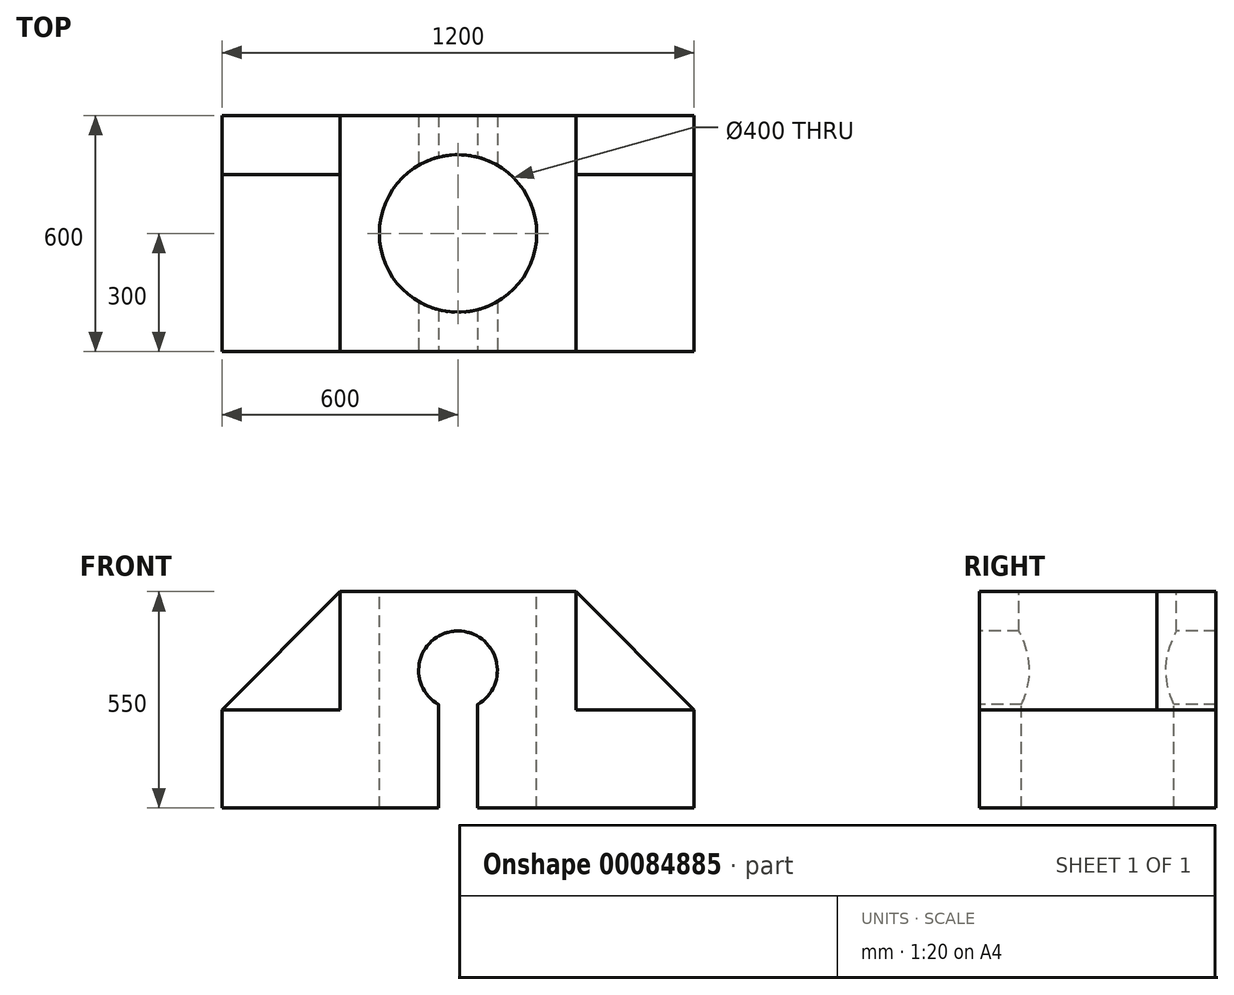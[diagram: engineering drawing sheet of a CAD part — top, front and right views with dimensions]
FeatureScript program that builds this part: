
annotation { "Feature Type Name" : "Feature", "Feature Type Description" : "" }
export const myFeature = defineFeature(function(context is Context, id is Id, definition is map)
    precondition{}
    {
        {
            var Q0;
            Q0=qCreatedBy(makeId("Front.planeOp"),FACE);
            var sketch = newSketch(context, id + "F0", { "sketchPlane" : qUnion([Q0])});
            skLineSegment(sketch, "E0.bottom", {"start": v(-600, -275) * mm, "end": v(600, -275) * mm});
            skLineSegment(sketch, "E0.top", {"start": v(-300, 275) * mm, "end": v(300, 275) * mm});
            skLineSegment(sketch, "E0.left", {"start": v(-600, -275) * mm, "end": v(-600, -25) * mm});
            skLineSegment(sketch, "E0.right", {"start": v(600, -275) * mm, "end": v(600, -25) * mm});
            skPoint(sketch, "E0.middle", {"position": v(0, 0) * mm});
            skLineSegment(sketch, "E1.top", {"start": v(600, -25) * mm, "end": v(300, -25) * mm});
            skLineSegment(sketch, "E1.right", {"start": v(300, 275) * mm, "end": v(300, -25) * mm});
            skLineSegment(sketch, "E2.top", {"start": v(-600, -25) * mm, "end": v(-300, -25) * mm});
            skLineSegment(sketch, "E2.right", {"start": v(-300, 275) * mm, "end": v(-300, -25) * mm});
            skPoint(sketch, "E3.orphan", {"position": v(-600, 275) * mm});
            skPoint(sketch, "E4.orphan", {"position": v(600, 275) * mm});
            skSolve(sketch);
        }
        {
            var Q0;
            Q0 = qSketchRegion(id + "F0", true);
            extrude(context, id + "F1", {"entities" : qUnion([Q0]), "depth" : 600 * mm});
        }
        {
            var Q0;
            Q0=makeQuery(id+"F1.opExtrude","CAP_FACE",FACE,{"disambiguationData":[OSD([sQuery(id+"F0.wireOp",EDGE,"E0.bottom"),sQuery(id+"F0.wireOp",EDGE,"E0.top"),sQuery(id+"F0.wireOp",EDGE,"E0.left"),sQuery(id+"F0.wireOp",EDGE,"E0.right"),sQuery(id+"F0.wireOp",EDGE,"E1.top"),sQuery(id+"F0.wireOp",EDGE,"E1.right"),sQuery(id+"F0.wireOp",EDGE,"E2.top"),sQuery(id+"F0.wireOp",EDGE,"E2.right")])],"isStart":true});
            var sketch = newSketch(context, id + "F2", { "sketchPlane" : qUnion([Q0])});
            skLineSegment(sketch, "E5", {"start": v(-300, 275) * mm, "end": v(-600, -25) * mm});
            skLineSegment(sketch, "E6", {"start": v(-600, -25) * mm, "end": v(-300, -25) * mm});
            skLineSegment(sketch, "E7", {"start": v(-300, -25) * mm, "end": v(-300, 275) * mm});
            skLineSegment(sketch, "E8", {"start": v(300, 275) * mm, "end": v(600, -25) * mm});
            skLineSegment(sketch, "E9", {"start": v(600, -25) * mm, "end": v(300, -25) * mm});
            skLineSegment(sketch, "E10", {"start": v(300, -25) * mm, "end": v(300, 275) * mm});
            skSolve(sketch);
        }
        {
            var Q0;
            Q0 = qSketchRegion(id + "F2", true);
            extrude(context, id + "F3", {"entities" : qUnion([Q0]), "operationType" : NewBodyOperationType.ADD, "oppositeDirection" : true, "depth" : 150 * mm});
        }
        {
            var Q0;
            Q0=makeQuery(id+"F1.opExtrude","CAP_FACE",FACE,{"disambiguationData":[OSD([sQuery(id+"F0.wireOp",EDGE,"E0.bottom"),sQuery(id+"F0.wireOp",EDGE,"E0.top"),sQuery(id+"F0.wireOp",EDGE,"E0.left"),sQuery(id+"F0.wireOp",EDGE,"E0.right"),sQuery(id+"F0.wireOp",EDGE,"E1.top"),sQuery(id+"F0.wireOp",EDGE,"E1.right"),sQuery(id+"F0.wireOp",EDGE,"E2.top"),sQuery(id+"F0.wireOp",EDGE,"E2.right")])],"isStart":false});
            var sketch = newSketch(context, id + "F4", { "sketchPlane" : qUnion([Q0])});
            skArc(sketch, "E11", {"start": v(50, -11.6) * mm, "mid": v(0, 175) * mm, "end": v(-50, -11.6) * mm});
            skLineSegment(sketch, "E12.bottom", {"start": v(-50, 75) * mm, "end": v(0, 75) * mm});
            skLineSegment(sketch, "E12.top", {"start": v(-50, -625) * mm, "end": v(50, -625) * mm});
            skLineSegment(sketch, "E12.left", {"start": v(-50, -11.6) * mm, "end": v(-50, -625) * mm});
            skLineSegment(sketch, "E12.right", {"start": v(50, -11.6) * mm, "end": v(50, -625) * mm});
            skPoint(sketch, "E12.middle", {"position": v(0, -275) * mm});
            skPoint(sketch, "E13.orphan", {"position": v(50, 75) * mm});
            skSolve(sketch);
        }
        {
            var Q0;
            Q0 = qSketchRegion(id + "F4", true);
            extrude(context, id + "F5", {"entities" : qUnion([Q0]), "operationType" : NewBodyOperationType.REMOVE, "endBound" : BoundingType.THROUGH_ALL, "oppositeDirection" : true, "depth" : 25 * mm});
        }
        {
            var Q0;
            Q0=makeQuery(id+"F1.opExtrude","SWEPT_FACE",FACE,{"disambiguationData":[OSD([sQuery(id+"F0.wireOp",EDGE,"E0.top")])]});
            var sketch = newSketch(context, id + "F6", { "sketchPlane" : qUnion([Q0])});
            skCircle(sketch, "E14", {"center": v(0, -300) * mm, "radius": 200 * mm});
            skSolve(sketch);
        }
        {
            var Q0;
            Q0 = qSketchRegion(id + "F6", true);
            extrude(context, id + "F7", {"entities" : qUnion([Q0]), "operationType" : NewBodyOperationType.REMOVE, "endBound" : BoundingType.THROUGH_ALL, "oppositeDirection" : true, "depth" : 25 * mm});
        }
    });
